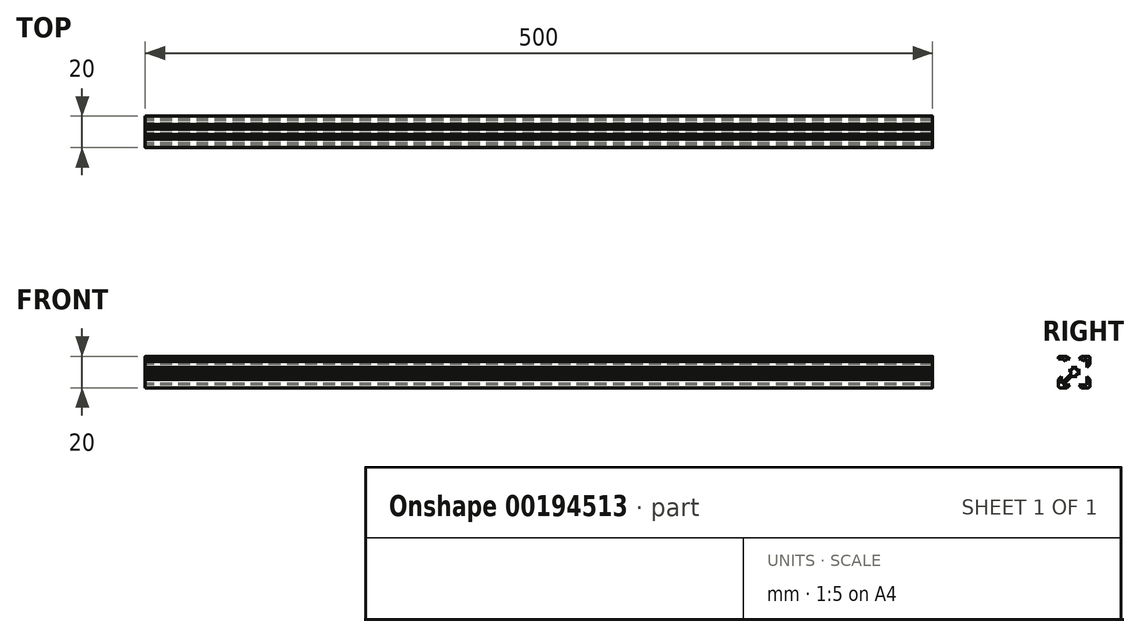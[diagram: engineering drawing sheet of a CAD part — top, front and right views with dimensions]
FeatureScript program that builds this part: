
annotation { "Feature Type Name" : "Feature", "Feature Type Description" : "" }
export const myFeature = defineFeature(function(context is Context, id is Id, definition is map)
    precondition{}
    {
        {
            var Q0;
            Q0=qCreatedBy(makeId("Right.planeOp"),FACE);
            var sketch = newSketch(context, id + "F0", { "sketchPlane" : qUnion([Q0])});
            skArc(sketch, "E0.filletArc", {"start": v(9, -10) * mm, "mid": v(9.7, -9.7) * mm, "end": v(10, -9) * mm});
            skArc(sketch, "E1", {"start": v(2.1, 0) * mm, "mid": v(1.48, -1.48) * mm, "end": v(0, -2.1) * mm});
            skLineSegment(sketch, "E2", {"start": v(0, -2.1) * mm, "end": v(0, -2.84) * mm});
            skLineSegment(sketch, "E3", {"start": v(2.1, 0) * mm, "end": v(2.84, 0) * mm});
            skLineSegment(sketch, "E4", {"start": v(2.84, -8.2) * mm, "end": v(4.64, -10) * mm});
            skLineSegment(sketch, "E5", {"start": v(8.2, -2.84) * mm, "end": v(10, -4.64) * mm});
            skLineSegment(sketch, "E6", {"start": v(4.64, -10) * mm, "end": v(9, -10) * mm});
            skLineSegment(sketch, "E7", {"start": v(10, -4.64) * mm, "end": v(10, -9) * mm});
            skLineSegment(sketch, "E8", {"start": v(2.84, -8.2) * mm, "end": v(10, -8.2) * mm});
            skLineSegment(sketch, "E9", {"start": v(8.2, -2.84) * mm, "end": v(8.2, -10) * mm});
            skLineSegment(sketch, "E10", {"start": v(9, -9) * mm, "end": v(8.2, -8.2) * mm});
            skPoint(sketch, "E11", {"position": v(8.73, -7.67) * mm});
            skPoint(sketch, "E12", {"position": v(7.67, -8.73) * mm});
            skPoint(sketch, "E13", {"position": v(8.2, -8.2) * mm});
            skPoint(sketch, "E14", {"position": v(5.53, -4.47) * mm});
            skPoint(sketch, "E15", {"position": v(4.47, -5.53) * mm});
            skLineSegment(sketch, "E16", {"start": v(7.67, -8.73) * mm, "end": v(4.47, -5.53) * mm});
            skLineSegment(sketch, "E17", {"start": v(8.73, -7.67) * mm, "end": v(5.53, -4.47) * mm});
            skLineSegment(sketch, "E18", {"start": v(5.53, -4.47) * mm, "end": v(1.92, -0.86) * mm});
            skLineSegment(sketch, "E19", {"start": v(4.47, -5.53) * mm, "end": v(0.86, -1.92) * mm});
            skLineSegment(sketch, "E20", {"start": v(8.2, -7.14) * mm, "end": v(8.2, -5.5) * mm});
            skLineSegment(sketch, "E21", {"start": v(7.14, -8.2) * mm, "end": v(5.5, -8.2) * mm});
            skLineSegment(sketch, "E22", {"start": v(5.5, -8.2) * mm, "end": v(5.5, -6.56) * mm});
            skLineSegment(sketch, "E23", {"start": v(8.2, -5.5) * mm, "end": v(6.56, -5.5) * mm});
            skLineSegment(sketch, "E24", {"start": v(2.84, 0) * mm, "end": v(2.84, -1.78) * mm});
            skLineSegment(sketch, "E25", {"start": v(0, -2.84) * mm, "end": v(1.78, -2.84) * mm});
            skArc(sketch, "E26.filletArc", {"start": v(10, 9) * mm, "mid": v(9.7, 9.7) * mm, "end": v(9, 10) * mm});
            skArc(sketch, "E27", {"start": v(0, 2.1) * mm, "mid": v(1.48, 1.48) * mm, "end": v(2.1, 0) * mm});
            skLineSegment(sketch, "E28", {"start": v(0, 2.1) * mm, "end": v(0, 2.84) * mm});
            skLineSegment(sketch, "E29", {"start": v(8.2, 2.84) * mm, "end": v(10, 4.64) * mm});
            skLineSegment(sketch, "E30", {"start": v(2.84, 8.2) * mm, "end": v(4.64, 10) * mm});
            skLineSegment(sketch, "E31", {"start": v(10, 4.64) * mm, "end": v(10, 9) * mm});
            skLineSegment(sketch, "E32", {"start": v(4.64, 10) * mm, "end": v(9, 10) * mm});
            skLineSegment(sketch, "E33", {"start": v(8.2, 2.84) * mm, "end": v(8.2, 10) * mm});
            skLineSegment(sketch, "E34", {"start": v(2.84, 8.2) * mm, "end": v(10, 8.2) * mm});
            skLineSegment(sketch, "E35", {"start": v(9, 9) * mm, "end": v(8.2, 8.2) * mm});
            skPoint(sketch, "E36", {"position": v(7.67, 8.73) * mm});
            skPoint(sketch, "E37", {"position": v(8.73, 7.67) * mm});
            skPoint(sketch, "E38", {"position": v(8.2, 8.2) * mm});
            skPoint(sketch, "E39", {"position": v(4.47, 5.53) * mm});
            skPoint(sketch, "E40", {"position": v(5.53, 4.47) * mm});
            skLineSegment(sketch, "E41", {"start": v(8.73, 7.67) * mm, "end": v(5.53, 4.47) * mm});
            skLineSegment(sketch, "E42", {"start": v(7.67, 8.73) * mm, "end": v(4.47, 5.53) * mm});
            skLineSegment(sketch, "E43", {"start": v(4.47, 5.53) * mm, "end": v(0.86, 1.92) * mm});
            skLineSegment(sketch, "E44", {"start": v(5.53, 4.47) * mm, "end": v(1.92, 0.86) * mm});
            skLineSegment(sketch, "E45", {"start": v(7.14, 8.2) * mm, "end": v(5.5, 8.2) * mm});
            skLineSegment(sketch, "E46", {"start": v(8.2, 7.14) * mm, "end": v(8.2, 5.5) * mm});
            skLineSegment(sketch, "E47", {"start": v(8.2, 5.5) * mm, "end": v(6.56, 5.5) * mm});
            skLineSegment(sketch, "E48", {"start": v(5.5, 8.2) * mm, "end": v(5.5, 6.56) * mm});
            skLineSegment(sketch, "E49", {"start": v(0, 2.84) * mm, "end": v(1.78, 2.84) * mm});
            skLineSegment(sketch, "E50", {"start": v(2.84, 0) * mm, "end": v(2.84, 1.78) * mm});
            skArc(sketch, "E51.filletArc", {"start": v(-9, 10) * mm, "mid": v(-9.7, 9.7) * mm, "end": v(-10, 9) * mm});
            skArc(sketch, "E52", {"start": v(-2.1, 0) * mm, "mid": v(-1.48, 1.48) * mm, "end": v(0, 2.1) * mm});
            skLineSegment(sketch, "E53", {"start": v(-2.1, 0) * mm, "end": v(-2.84, 0) * mm});
            skLineSegment(sketch, "E54", {"start": v(-2.84, 8.2) * mm, "end": v(-4.64, 10) * mm});
            skLineSegment(sketch, "E55", {"start": v(-8.2, 2.84) * mm, "end": v(-10, 4.64) * mm});
            skLineSegment(sketch, "E56", {"start": v(-4.64, 10) * mm, "end": v(-9, 10) * mm});
            skLineSegment(sketch, "E57", {"start": v(-10, 4.64) * mm, "end": v(-10, 9) * mm});
            skLineSegment(sketch, "E58", {"start": v(-2.84, 8.2) * mm, "end": v(-10, 8.2) * mm});
            skLineSegment(sketch, "E59", {"start": v(-8.2, 2.84) * mm, "end": v(-8.2, 10) * mm});
            skLineSegment(sketch, "E60", {"start": v(-9, 9) * mm, "end": v(-8.2, 8.2) * mm});
            skPoint(sketch, "E61", {"position": v(-8.73, 7.67) * mm});
            skPoint(sketch, "E62", {"position": v(-7.67, 8.73) * mm});
            skPoint(sketch, "E63", {"position": v(-8.2, 8.2) * mm});
            skPoint(sketch, "E64", {"position": v(-5.53, 4.47) * mm});
            skPoint(sketch, "E65", {"position": v(-4.47, 5.53) * mm});
            skLineSegment(sketch, "E66", {"start": v(-7.67, 8.73) * mm, "end": v(-4.47, 5.53) * mm});
            skLineSegment(sketch, "E67", {"start": v(-8.73, 7.67) * mm, "end": v(-5.53, 4.47) * mm});
            skLineSegment(sketch, "E68", {"start": v(-5.53, 4.47) * mm, "end": v(-1.92, 0.86) * mm});
            skLineSegment(sketch, "E69", {"start": v(-4.47, 5.53) * mm, "end": v(-0.86, 1.92) * mm});
            skLineSegment(sketch, "E70", {"start": v(-8.2, 7.14) * mm, "end": v(-8.2, 5.5) * mm});
            skLineSegment(sketch, "E71", {"start": v(-7.14, 8.2) * mm, "end": v(-5.5, 8.2) * mm});
            skLineSegment(sketch, "E72", {"start": v(-5.5, 8.2) * mm, "end": v(-5.5, 6.56) * mm});
            skLineSegment(sketch, "E73", {"start": v(-8.2, 5.5) * mm, "end": v(-6.56, 5.5) * mm});
            skLineSegment(sketch, "E74", {"start": v(-2.84, 0) * mm, "end": v(-2.84, 1.78) * mm});
            skLineSegment(sketch, "E75", {"start": v(0, 2.84) * mm, "end": v(-1.78, 2.84) * mm});
            skArc(sketch, "E76.filletArc", {"start": v(-10, -9) * mm, "mid": v(-9.7, -9.7) * mm, "end": v(-9, -10) * mm});
            skArc(sketch, "E77", {"start": v(0, -2.1) * mm, "mid": v(-1.48, -1.48) * mm, "end": v(-2.1, 0) * mm});
            skLineSegment(sketch, "E78", {"start": v(-8.2, -2.84) * mm, "end": v(-10, -4.64) * mm});
            skLineSegment(sketch, "E79", {"start": v(-2.84, -8.2) * mm, "end": v(-4.64, -10) * mm});
            skLineSegment(sketch, "E80", {"start": v(-10, -4.64) * mm, "end": v(-10, -9) * mm});
            skLineSegment(sketch, "E81", {"start": v(-4.64, -10) * mm, "end": v(-9, -10) * mm});
            skLineSegment(sketch, "E82", {"start": v(-8.2, -2.84) * mm, "end": v(-8.2, -10) * mm});
            skLineSegment(sketch, "E83", {"start": v(-2.84, -8.2) * mm, "end": v(-10, -8.2) * mm});
            skLineSegment(sketch, "E84", {"start": v(-9, -9) * mm, "end": v(-8.2, -8.2) * mm});
            skPoint(sketch, "E85", {"position": v(-7.67, -8.73) * mm});
            skPoint(sketch, "E86", {"position": v(-8.73, -7.67) * mm});
            skPoint(sketch, "E87", {"position": v(-8.2, -8.2) * mm});
            skPoint(sketch, "E88", {"position": v(-4.47, -5.53) * mm});
            skPoint(sketch, "E89", {"position": v(-5.53, -4.47) * mm});
            skLineSegment(sketch, "E90", {"start": v(-8.73, -7.67) * mm, "end": v(-5.53, -4.47) * mm});
            skLineSegment(sketch, "E91", {"start": v(-7.67, -8.73) * mm, "end": v(-4.47, -5.53) * mm});
            skLineSegment(sketch, "E92", {"start": v(-4.47, -5.53) * mm, "end": v(-0.86, -1.92) * mm});
            skLineSegment(sketch, "E93", {"start": v(-5.53, -4.47) * mm, "end": v(-1.92, -0.86) * mm});
            skLineSegment(sketch, "E94", {"start": v(-7.14, -8.2) * mm, "end": v(-5.5, -8.2) * mm});
            skLineSegment(sketch, "E95", {"start": v(-8.2, -7.14) * mm, "end": v(-8.2, -5.5) * mm});
            skLineSegment(sketch, "E96", {"start": v(-8.2, -5.5) * mm, "end": v(-6.56, -5.5) * mm});
            skLineSegment(sketch, "E97", {"start": v(-5.5, -8.2) * mm, "end": v(-5.5, -6.56) * mm});
            skLineSegment(sketch, "E98", {"start": v(0, -2.84) * mm, "end": v(-1.78, -2.84) * mm});
            skLineSegment(sketch, "E99", {"start": v(-2.84, 0) * mm, "end": v(-2.84, -1.78) * mm});
            skLineSegment(sketch, "E100", {"start": v(-1.78, -2.84) * mm, "end": v(-2.84, -1.78) * mm});
            skLineSegment(sketch, "E101", {"start": v(-10, 8.2) * mm, "end": v(-10, 9) * mm});
            skLineSegment(sketch, "E102", {"start": v(-9, 10) * mm, "end": v(-4.64, 10) * mm});
            skLineSegment(sketch, "E103", {"start": v(-2.84, 8.2) * mm, "end": v(-7.14, 8.2) * mm});
            skLineSegment(sketch, "E104", {"start": v(-1.78, 2.84) * mm, "end": v(1.78, 2.84) * mm});
            skLineSegment(sketch, "E105", {"start": v(7.14, 8.2) * mm, "end": v(2.84, 8.2) * mm});
            skLineSegment(sketch, "E106", {"start": v(10, 9) * mm, "end": v(10, 4.64) * mm});
            skLineSegment(sketch, "E107", {"start": v(8.2, 2.84) * mm, "end": v(8.2, 5.5) * mm});
            skSolve(sketch);
        }
        {
            var Q0;
            {var subQ5=sQuery(id+"F0.wireOp",EDGE,"E0.filletArc");Q0=makeQuery(id+"F0.imprint","IMPRINT",FACE,{"disambiguationData":[TD([[makeQuery(id+"F0.imprint","IMPRINT",EDGE,{"derivedFrom":subQ5}),1.0]])]});}
            var Q1;
            {var subQ0=sQuery(id+"F0.wireOp",EDGE,"E21");Q1=makeQuery(id+"F0.imprint","IMPRINT",FACE,{"disambiguationData":[TD([[makeQuery(id+"F0.imprint","IMPRINT",EDGE,{"derivedFrom":subQ0}),-1.0]])]});}
            var Q2;
            {var subQ0=sQuery(id+"F0.wireOp",EDGE,"E20");Q2=makeQuery(id+"F0.imprint","IMPRINT",FACE,{"disambiguationData":[TD([[makeQuery(id+"F0.imprint","IMPRINT",EDGE,{"derivedFrom":subQ0}),1.0]])]});}
            var Q3;
            {var subQ6=sQuery(id+"F0.wireOp",EDGE,"E26.filletArc");Q3=makeQuery(id+"F0.imprint","IMPRINT",FACE,{"disambiguationData":[TD([[makeQuery(id+"F0.imprint","IMPRINT",EDGE,{"derivedFrom":subQ6}),1.0]])]});}
            var Q4;
            {var subQ0=sQuery(id+"F0.wireOp",EDGE,"E46");Q4=makeQuery(id+"F0.imprint","IMPRINT",FACE,{"disambiguationData":[TD([[makeQuery(id+"F0.imprint","IMPRINT",EDGE,{"derivedFrom":subQ0}),-1.0]])]});}
            var Q5;
            {var subQ3=sQuery(id+"F0.wireOp",EDGE,"E48");Q5=makeQuery(id+"F0.imprint","IMPRINT",FACE,{"disambiguationData":[TD([[makeQuery(id+"F0.imprint","IMPRINT",EDGE,{"derivedFrom":subQ3}),1.0]])]});}
            var Q6;
            {var subQ6=sQuery(id+"F0.wireOp",EDGE,"E51.filletArc");Q6=makeQuery(id+"F0.imprint","IMPRINT",FACE,{"disambiguationData":[TD([[makeQuery(id+"F0.imprint","IMPRINT",EDGE,{"derivedFrom":subQ6}),1.0]])]});}
            var Q7;
            {var subQ3=sQuery(id+"F0.wireOp",EDGE,"E72");Q7=makeQuery(id+"F0.imprint","IMPRINT",FACE,{"disambiguationData":[TD([[makeQuery(id+"F0.imprint","IMPRINT",EDGE,{"derivedFrom":subQ3}),-1.0]])]});}
            var Q8;
            {var subQ0=sQuery(id+"F0.wireOp",EDGE,"E70");Q8=makeQuery(id+"F0.imprint","IMPRINT",FACE,{"disambiguationData":[TD([[makeQuery(id+"F0.imprint","IMPRINT",EDGE,{"derivedFrom":subQ0}),1.0]])]});}
            var Q9;
            {var subQ5=sQuery(id+"F0.wireOp",EDGE,"E76.filletArc");Q9=makeQuery(id+"F0.imprint","IMPRINT",FACE,{"disambiguationData":[TD([[makeQuery(id+"F0.imprint","IMPRINT",EDGE,{"derivedFrom":subQ5}),1.0]])]});}
            var Q10;
            {var subQ0=sQuery(id+"F0.wireOp",EDGE,"E95");Q10=makeQuery(id+"F0.imprint","IMPRINT",FACE,{"disambiguationData":[TD([[makeQuery(id+"F0.imprint","IMPRINT",EDGE,{"derivedFrom":subQ0}),-1.0]])]});}
            var Q11;
            {var subQ0=sQuery(id+"F0.wireOp",EDGE,"E94");Q11=makeQuery(id+"F0.imprint","IMPRINT",FACE,{"disambiguationData":[TD([[makeQuery(id+"F0.imprint","IMPRINT",EDGE,{"derivedFrom":subQ0}),1.0]])]});}
            var Q12;
            {var subQ4=sQuery(id+"F0.wireOp",EDGE,"E24");Q12=makeQuery(id+"F0.imprint","IMPRINT",FACE,{"disambiguationData":[TD([[makeQuery(id+"F0.imprint","IMPRINT",EDGE,{"derivedFrom":subQ4}),-1.0]])]});}
            var Q13;
            {var subQ4=sQuery(id+"F0.wireOp",EDGE,"E25");Q13=makeQuery(id+"F0.imprint","IMPRINT",FACE,{"disambiguationData":[TD([[makeQuery(id+"F0.imprint","IMPRINT",EDGE,{"derivedFrom":subQ4}),1.0]])]});}
            var Q14;
            {var subQ0=sQuery(id+"F0.wireOp",EDGE,"E2");Q14=makeQuery(id+"F0.imprint","IMPRINT",FACE,{"disambiguationData":[TD([[makeQuery(id+"F0.imprint","IMPRINT",EDGE,{"derivedFrom":subQ0}),1.0]])]});}
            var Q15;
            {var subQ0=sQuery(id+"F0.wireOp",EDGE,"E2");Q15=makeQuery(id+"F0.imprint","IMPRINT",FACE,{"disambiguationData":[TD([[makeQuery(id+"F0.imprint","IMPRINT",EDGE,{"derivedFrom":subQ0}),-1.0]])]});}
            var Q16;
            {var subQ4=sQuery(id+"F0.wireOp",EDGE,"E4");Q16=makeQuery(id+"F0.imprint","IMPRINT",FACE,{"disambiguationData":[TD([[makeQuery(id+"F0.imprint","IMPRINT",EDGE,{"derivedFrom":subQ4}),1.0]])]});}
            var Q17;
            {var subQ1=sQuery(id+"F0.wireOp",EDGE,"E5");Q17=makeQuery(id+"F0.imprint","IMPRINT",FACE,{"disambiguationData":[TD([[makeQuery(id+"F0.imprint","IMPRINT",EDGE,{"derivedFrom":subQ1}),-1.0]])]});}
            var Q18;
            {var subQ0=sQuery(id+"F0.wireOp",EDGE,"E28");Q18=makeQuery(id+"F0.imprint","IMPRINT",FACE,{"disambiguationData":[TD([[makeQuery(id+"F0.imprint","IMPRINT",EDGE,{"derivedFrom":subQ0}),-1.0]])]});}
            var Q19;
            {var subQ0=sQuery(id+"F0.wireOp",EDGE,"E3");Q19=makeQuery(id+"F0.imprint","IMPRINT",FACE,{"disambiguationData":[TD([[makeQuery(id+"F0.imprint","IMPRINT",EDGE,{"derivedFrom":subQ0}),1.0]])]});}
            var Q20;
            {var subQ0=sQuery(id+"F0.wireOp",EDGE,"E28");Q20=makeQuery(id+"F0.imprint","IMPRINT",FACE,{"disambiguationData":[TD([[makeQuery(id+"F0.imprint","IMPRINT",EDGE,{"derivedFrom":subQ0}),1.0]])]});}
            var Q21;
            {var subQ0=sQuery(id+"F0.wireOp",EDGE,"E28");Q21=makeQuery(id+"F0.imprint","IMPRINT",FACE,{"disambiguationData":[TD([[makeQuery(id+"F0.imprint","IMPRINT",EDGE,{"derivedFrom":subQ0}),-1.0]])]});}
            var Q22;
            {var subQ5=sQuery(id+"F0.wireOp",EDGE,"E29");Q22=makeQuery(id+"F0.imprint","IMPRINT",FACE,{"disambiguationData":[TD([[makeQuery(id+"F0.imprint","IMPRINT",EDGE,{"derivedFrom":subQ5}),1.0]])]});}
            var Q23;
            {var subQ4=sQuery(id+"F0.wireOp",EDGE,"E30");Q23=makeQuery(id+"F0.imprint","IMPRINT",FACE,{"disambiguationData":[TD([[makeQuery(id+"F0.imprint","IMPRINT",EDGE,{"derivedFrom":subQ4}),-1.0]])]});}
            var Q24;
            {var subQ4=sQuery(id+"F0.wireOp",EDGE,"E74");Q24=makeQuery(id+"F0.imprint","IMPRINT",FACE,{"disambiguationData":[TD([[makeQuery(id+"F0.imprint","IMPRINT",EDGE,{"derivedFrom":subQ4}),-1.0]])]});}
            var Q25;
            {var subQ1=sQuery(id+"F0.wireOp",EDGE,"E54");Q25=makeQuery(id+"F0.imprint","IMPRINT",FACE,{"disambiguationData":[TD([[makeQuery(id+"F0.imprint","IMPRINT",EDGE,{"derivedFrom":subQ1}),1.0]])]});}
            var Q26;
            {var subQ5=sQuery(id+"F0.wireOp",EDGE,"E57");Q26=makeQuery(id+"F0.imprint","IMPRINT",FACE,{"disambiguationData":[TD([[makeQuery(id+"F0.imprint","IMPRINT",EDGE,{"derivedFrom":subQ5}),-1.0]])]});}
            var Q27;
            {var subQ0=sQuery(id+"F0.wireOp",EDGE,"E53");Q27=makeQuery(id+"F0.imprint","IMPRINT",FACE,{"disambiguationData":[TD([[makeQuery(id+"F0.imprint","IMPRINT",EDGE,{"derivedFrom":subQ0}),1.0]])]});}
            var Q28;
            {var subQ4=sQuery(id+"F0.wireOp",EDGE,"E78");Q28=makeQuery(id+"F0.imprint","IMPRINT",FACE,{"disambiguationData":[TD([[makeQuery(id+"F0.imprint","IMPRINT",EDGE,{"derivedFrom":subQ4}),1.0]])]});}
            var Q29;
            {var subQ1=sQuery(id+"F0.wireOp",EDGE,"E79");Q29=makeQuery(id+"F0.imprint","IMPRINT",FACE,{"disambiguationData":[TD([[makeQuery(id+"F0.imprint","IMPRINT",EDGE,{"derivedFrom":subQ1}),-1.0]])]});}
            var Q30;
            {var subQ5=sQuery(id+"F0.wireOp",EDGE,"E100");Q30=makeQuery(id+"F0.imprint","IMPRINT",FACE,{"disambiguationData":[TD([[makeQuery(id+"F0.imprint","IMPRINT",EDGE,{"derivedFrom":subQ5}),-1.0]])]});}
            var Q31;
            {var subQ6=sQuery(id+"F0.wireOp",EDGE,"E100");Q31=makeQuery(id+"F0.imprint","IMPRINT",FACE,{"disambiguationData":[TD([[makeQuery(id+"F0.imprint","IMPRINT",EDGE,{"derivedFrom":subQ6}),1.0]])]});}
            var Q32;
            {var subQ0=sQuery(id+"F0.wireOp",EDGE,"E18");var subQ15=sQuery(id+"F0.wireOp",EDGE,"E1");var subQ16=makeQuery(id+"F0.imprint","INTERSECT",VERTEX,{"derivedFrom":[subQ15,subQ0]});Q32=makeQuery(id+"F0.imprint","IMPRINT",FACE,{"disambiguationData":[TD([[makeQuery(id+"F0.imprint","IMPRINT",EDGE,{"disambiguationData":[TD([[subQ16,-1.0]])],"derivedFrom":subQ15}),1.0]])]});}
            var Q33;
            {var subQ4=sQuery(id+"F0.wireOp",EDGE,"E43");var subQ5=sQuery(id+"F0.wireOp",EDGE,"E27");var subQ6=makeQuery(id+"F0.imprint","INTERSECT",VERTEX,{"derivedFrom":[subQ5,subQ4]});Q33=makeQuery(id+"F0.imprint","IMPRINT",FACE,{"disambiguationData":[TD([[makeQuery(id+"F0.imprint","IMPRINT",EDGE,{"disambiguationData":[TD([[subQ6,-1.0]])],"derivedFrom":subQ5}),1.0]])]});}
            var Q34;
            {var subQ0=sQuery(id+"F0.wireOp",EDGE,"E68");var subQ9=sQuery(id+"F0.wireOp",EDGE,"E52");var subQ10=makeQuery(id+"F0.imprint","INTERSECT",VERTEX,{"derivedFrom":[subQ9,subQ0]});Q34=makeQuery(id+"F0.imprint","IMPRINT",FACE,{"disambiguationData":[TD([[makeQuery(id+"F0.imprint","IMPRINT",EDGE,{"disambiguationData":[TD([[subQ10,-1.0]])],"derivedFrom":subQ9}),1.0]])]});}
            var Q35;
            Q35=sQuery(id+"F0.wireOp",EDGE,"E1");
            var Q36;
            Q36=sQuery(id+"F0.wireOp",EDGE,"E77");
            var Q37;
            Q37=sQuery(id+"F0.wireOp",EDGE,"E52");
            var Q38;
            Q38=sQuery(id+"F0.wireOp",EDGE,"E27");
            var Q39;
            Q39=sQuery(id+"F0.wireOp",EDGE,"E44");
            var Q40;
            Q40=sQuery(id+"F0.wireOp",EDGE,"E41");
            var Q41;
            Q41=sQuery(id+"F0.wireOp",EDGE,"E47");
            var Q42;
            Q42=sQuery(id+"F0.wireOp",EDGE,"E107");
            var Q43;
            Q43=sQuery(id+"F0.wireOp",EDGE,"E29");
            var Q44;
            Q44=sQuery(id+"F0.wireOp",EDGE,"E106");
            var Q45;
            Q45=sQuery(id+"F0.wireOp",EDGE,"E26.filletArc");
            var Q46;
            Q46=sQuery(id+"F0.wireOp",EDGE,"E32");
            var Q47;
            Q47=sQuery(id+"F0.wireOp",EDGE,"E30");
            var Q48;
            Q48=sQuery(id+"F0.wireOp",EDGE,"E34");
            var Q49;
            Q49=sQuery(id+"F0.wireOp",EDGE,"E48");
            var Q50;
            Q50=sQuery(id+"F0.wireOp",EDGE,"E42");
            var Q51;
            Q51=sQuery(id+"F0.wireOp",EDGE,"E43");
            var Q52;
            Q52=sQuery(id+"F0.wireOp",EDGE,"E104");
            var Q53;
            Q53=sQuery(id+"F0.wireOp",EDGE,"E69");
            var Q54;
            Q54=sQuery(id+"F0.wireOp",EDGE,"E66");
            var Q55;
            Q55=sQuery(id+"F0.wireOp",EDGE,"E72");
            var Q56;
            Q56=sQuery(id+"F0.wireOp",EDGE,"E58");
            var Q57;
            Q57=sQuery(id+"F0.wireOp",EDGE,"E54");
            var Q58;
            Q58=sQuery(id+"F0.wireOp",EDGE,"E56");
            var Q59;
            Q59=sQuery(id+"F0.wireOp",EDGE,"E51.filletArc");
            var Q60;
            Q60=sQuery(id+"F0.wireOp",EDGE,"E57");
            var Q61;
            Q61=sQuery(id+"F0.wireOp",EDGE,"E55");
            extrude(context, id + "F1", {"entities" : qUnion([Q0, Q1, Q2, Q3, Q4, Q5, Q6, Q7, Q8, Q9, Q10, Q11, Q12, Q13, Q14, Q15, Q16, Q17, Q18, Q19, Q20, Q21, Q22, Q23, Q24, Q25, Q26, Q27, Q28, Q29, Q30, Q31, Q32, Q33, Q34]), "surfaceEntities" : qUnion([Q35, Q36, Q37, Q38, Q39, Q40, Q41, Q42, Q43, Q44, Q45, Q46, Q47, Q48, Q49, Q50, Q51, Q52, Q53, Q54, Q55, Q56, Q57, Q58, Q59, Q60, Q61]), "depth" : 500 * mm});
        }
    });
